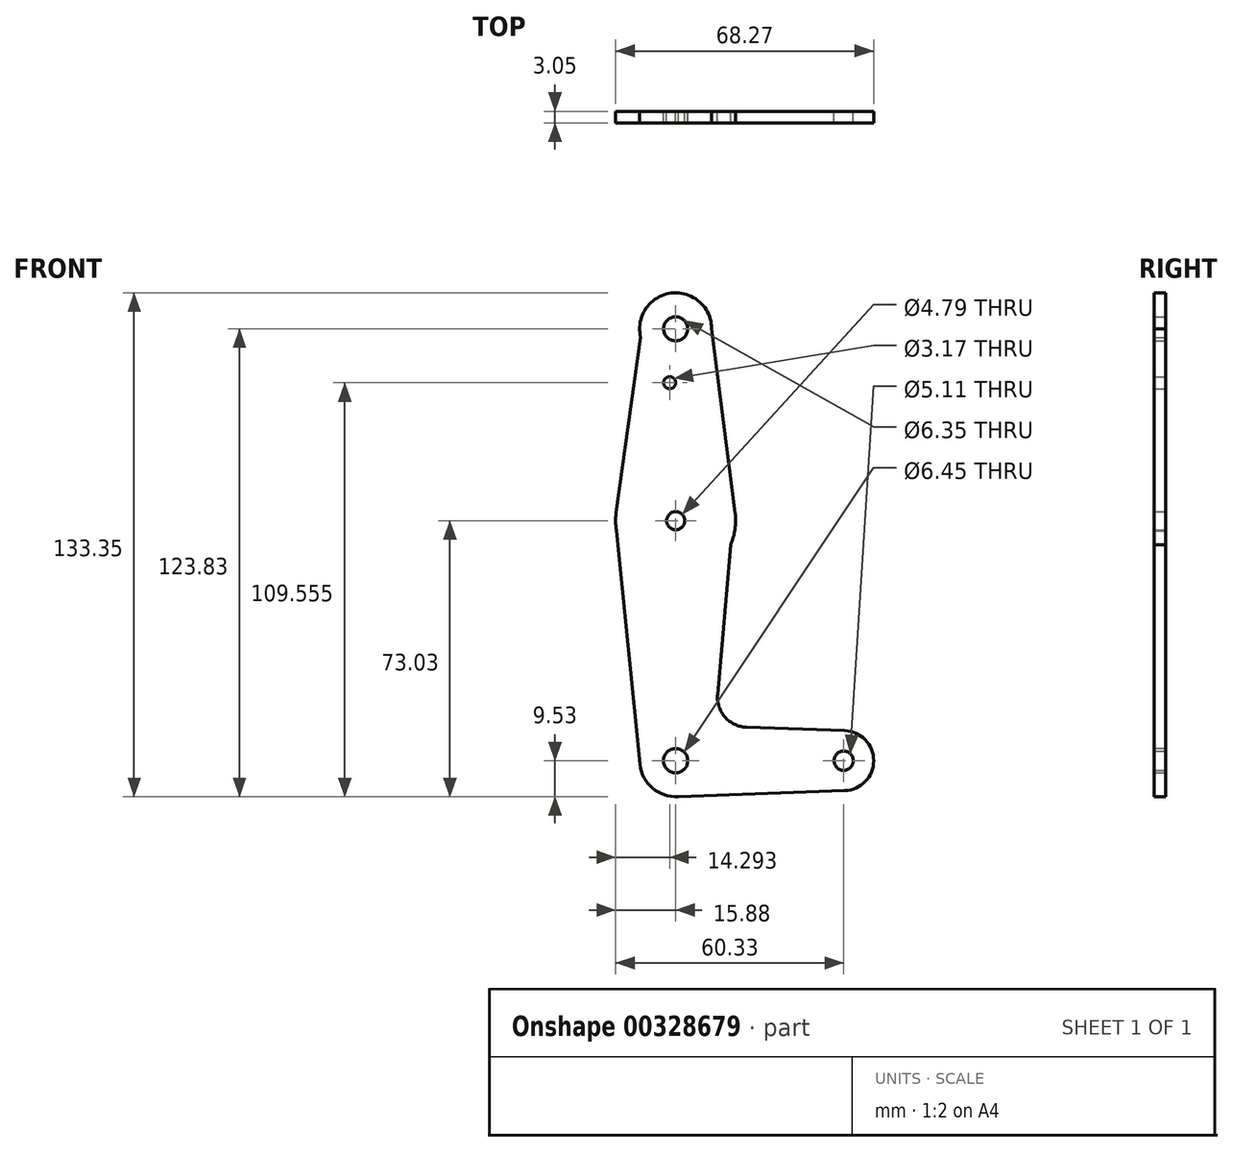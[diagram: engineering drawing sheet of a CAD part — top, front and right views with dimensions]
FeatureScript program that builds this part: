
annotation { "Feature Type Name" : "Feature", "Feature Type Description" : "" }
export const myFeature = defineFeature(function(context is Context, id is Id, definition is map)
    precondition{}
    {
        {
            var Q0;
            Q0=qCreatedBy(makeId("Front.planeOp"),FACE);
            var sketch = newSketch(context, id + "F0", { "sketchPlane" : qUnion([Q0])});
            skLineSegment(sketch, "E0", {"start": v(0, 50.8) * mm, "end": v(0, -63.5) * mm, "construction": true});
            skCircle(sketch, "E1", {"center": v(0, 50.8) * mm, "radius": 9.53 * mm});
            skCircle(sketch, "E2", {"center": v(0, 0) * mm, "radius": 15.88 * mm});
            skLineSegment(sketch, "E3", {"start": v(0, -63.5) * mm, "end": v(44.45, -63.5) * mm, "construction": true});
            skCircle(sketch, "E4", {"center": v(0, -63.5) * mm, "radius": 9.53 * mm});
            skCircle(sketch, "E5", {"center": v(44.45, -63.5) * mm, "radius": 7.94 * mm});
            skLineSegment(sketch, "E6", {"start": v(9.52, 50.8) * mm, "end": v(16, 0) * mm});
            skLineSegment(sketch, "E7", {"start": v(-9.25, 48.53) * mm, "end": v(-16.03, 0) * mm});
            skLineSegment(sketch, "E8", {"start": v(14.55, -6.35) * mm, "end": v(11.09, -46) * mm});
            skPoint(sketch, "E8.startSnap0", {"position": v(0, -6.35) * mm});
            skLineSegment(sketch, "E9", {"start": v(-15.64, -2.7) * mm, "end": v(-9.48, -64.45) * mm});
            skLineSegment(sketch, "E10", {"start": v(18.73, -54.64) * mm, "end": v(44.73, -55.57) * mm});
            skLineSegment(sketch, "E11", {"start": v(0, -73.02) * mm, "end": v(44.73, -71.43) * mm});
            skCircle(sketch, "E12", {"center": v(0, 50.8) * mm, "radius": 3.18 * mm});
            skCircle(sketch, "E13", {"center": v(0, 0) * mm, "radius": 2.4 * mm});
            skCircle(sketch, "E14", {"center": v(0, -63.5) * mm, "radius": 3.23 * mm});
            skCircle(sketch, "E15", {"center": v(44.45, -63.5) * mm, "radius": 2.56 * mm});
            skCircle(sketch, "E16", {"center": v(-1.59, 36.53) * mm, "radius": 1.59 * mm});
            skArc(sketch, "E17.filletArc", {"start": v(11.09, -46) * mm, "mid": v(13.05, -51.96) * mm, "end": v(18.73, -54.64) * mm});
            skSolve(sketch);
        }
        {
            var Q0;
            Q0 = qSketchRegion(id + "F0", true);
            extrude(context, id + "F1", {"entities" : qUnion([Q0]), "depth" : 3.05 * mm});
        }
    });
